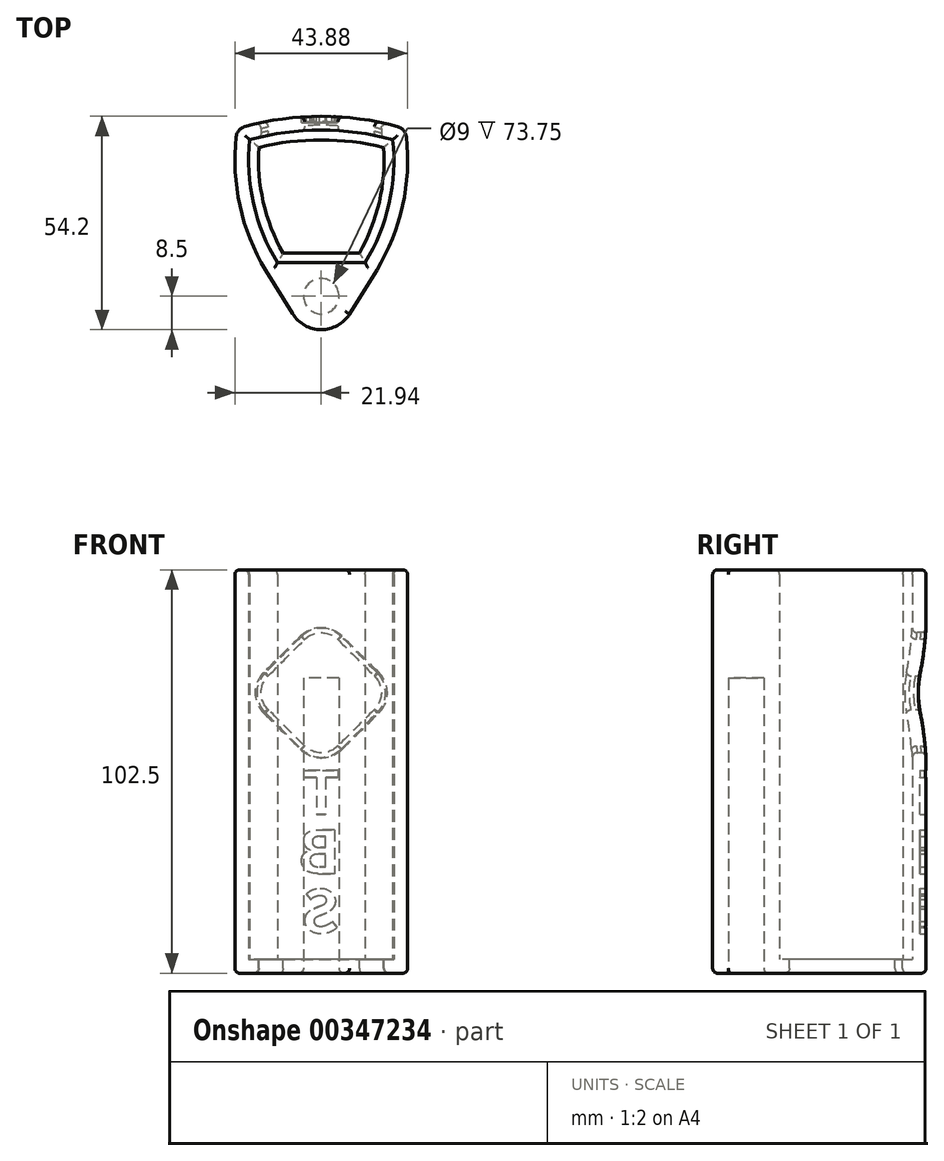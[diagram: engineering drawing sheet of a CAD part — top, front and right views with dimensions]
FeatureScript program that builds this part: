
annotation { "Feature Type Name" : "Feature", "Feature Type Description" : "" }
export const myFeature = defineFeature(function(context is Context, id is Id, definition is map)
    precondition{}
    {
        {
            var Q0;
            Q0=qCreatedBy(makeId("Top.planeOp"),FACE);
            var sketch = newSketch(context, id + "F0", { "sketchPlane" : qUnion([Q0])});
            skLineSegment(sketch, "E0", {"start": v(0, 0) * mm, "end": v(11.12, 0) * mm});
            skLineSegment(sketch, "E1", {"start": v(11.12, 0) * mm, "end": v(-11.12, 0) * mm});
            skArc(sketch, "E2", {"start": v(-18.16, 31.28) * mm, "mid": v(-17.22, 15.06) * mm, "end": v(-11.13, 0) * mm});
            skArc(sketch, "E3", {"start": v(11.13, 0) * mm, "mid": v(17.22, 15.06) * mm, "end": v(18.16, 31.28) * mm});
            skArc(sketch, "E4", {"start": v(18.16, 31.28) * mm, "mid": v(0, 33.7) * mm, "end": v(-18.16, 31.28) * mm});
            skArc(sketch, "E5.0", {"start": v(-21.34, 34) * mm, "mid": v(-20.88, 15.46) * mm, "end": v(-14.11, -1.82) * mm});
            skArc(sketch, "E5.1", {"start": v(21.34, 34) * mm, "mid": v(0, 37.2) * mm, "end": v(-21.34, 34) * mm});
            skArc(sketch, "E5.2", {"start": v(14.11, -1.82) * mm, "mid": v(20.88, 15.46) * mm, "end": v(21.34, 34) * mm});
            skCircle(sketch, "E6", {"center": v(0, -8.5) * mm, "radius": 4.5 * mm});
            skLineSegment(sketch, "E7", {"start": v(-14.11, -1.82) * mm, "end": v(-7.23, -12.97) * mm});
            skLineSegment(sketch, "E8", {"start": v(7.19, -13.03) * mm, "end": v(14.11, -1.82) * mm});
            skArc(sketch, "E9", {"start": v(-7.23, -12.97) * mm, "mid": v(-0.04, -17) * mm, "end": v(7.19, -13.03) * mm});
            skLineSegment(sketch, "E10", {"start": v(21.34, 34) * mm, "end": v(21.34, 39.15) * mm});
            skLineSegment(sketch, "E11", {"start": v(21.34, 39.15) * mm, "end": v(-21.34, 39.15) * mm});
            skLineSegment(sketch, "E12", {"start": v(-21.34, 39.15) * mm, "end": v(-21.34, 34) * mm});
            skSolve(sketch);
        }
        {
            var Q0;
            {var subQ3=sQuery(id+"F0.wireOp",EDGE,"E2");Q0=makeQuery(id+"F0.imprint","IMPRINT",FACE,{"disambiguationData":[TD([[makeQuery(id+"F0.imprint","IMPRINT",EDGE,{"derivedFrom":subQ3}),-1.0]])]});}
            var Q1;
            Q1=makeQuery(id+"F0.imprint","IMPRINT",FACE,{"disambiguationData":[TD([[makeQuery(id+"F0.imprint","IMPRINT",EDGE,{"derivedFrom":sQuery(id+"F0.wireOp",EDGE,"E6")}),1.0]])]});
            extrude(context, id + "F1", {"entities" : qUnion([Q0, Q1]), "depth" : 102.5 * mm});
        }
        {
            var Q0;
            {var subQ1=sQuery(id+"F0.wireOp",EDGE,"E2");Q0=makeQuery(id+"F0.imprint","IMPRINT",FACE,{"disambiguationData":[TD([[makeQuery(id+"F0.imprint","IMPRINT",EDGE,{"derivedFrom":subQ1}),1.0]])]});}
            extrude(context, id + "F2", {"entities" : qUnion([Q0]), "operationType" : NewBodyOperationType.ADD, "depth" : 3.5 * mm});
        }
        {
            var Q0;
            Q0=makeQuery(id+"F0.imprint","IMPRINT",FACE,{"disambiguationData":[TD([[makeQuery(id+"F0.imprint","IMPRINT",EDGE,{"derivedFrom":sQuery(id+"F0.wireOp",EDGE,"E6")}),1.0]])]});
            extrude(context, id + "F3", {"entities" : qUnion([Q0]), "operationType" : NewBodyOperationType.REMOVE, "depth" : 75 * mm});
        }
        {
            var Q0;
            Q0=makeQuery(id+"F0.imprint","IMPRINT",FACE,{"disambiguationData":[TD([[makeQuery(id+"F0.imprint","IMPRINT",EDGE,{"derivedFrom":sQuery(id+"F0.wireOp",EDGE,"E5.1")}),-1.0]])]});
            extrude(context, id + "F4", {"entities" : qUnion([Q0]), "operationType" : NewBodyOperationType.ADD, "depth" : 102.5 * mm});
        }
        {
            var Q0;
            Q0=makeQuery(id+"F4.opExtrude","SWEPT_FACE",FACE,{"disambiguationData":[OSD([sQuery(id+"F0.wireOp",EDGE,"E11")])]});
            var sketch = newSketch(context, id + "F5", { "sketchPlane" : qUnion([Q0])});
            skPoint(sketch, "E13.endSnap0", {"position": v(0, 0) * mm});
            skLineSegment(sketch, "E14", {"start": v(-17.75, 71.25) * mm, "end": v(0, 89) * mm});
            skLineSegment(sketch, "E15", {"start": v(17.75, 71.25) * mm, "end": v(0, 53.5) * mm});
            skLineSegment(sketch, "E16", {"start": v(0, 53.5) * mm, "end": v(-17.75, 71.25) * mm});
            skLineSegment(sketch, "E17", {"start": v(0, 89) * mm, "end": v(17.75, 71.25) * mm});
            skSolve(sketch);
        }
        {
            var Q0;
            Q0=makeQuery(id+"F5.imprint","IMPRINT",FACE,{"disambiguationData":[TD([[makeQuery(id+"F5.imprint","IMPRINT",EDGE,{"derivedFrom":sQuery(id+"F5.wireOp",EDGE,"E14")}),-1.0]])]});
            extrude(context, id + "F6", {"entities" : qUnion([Q0]), "operationType" : NewBodyOperationType.REMOVE, "oppositeDirection" : true, "depth" : 10 * mm});
        }
        {
            var Q0;
            Q0=makeQuery(id+"F6.boolean.opBoolean","COPY",EDGE,{"derivedFrom":makeQuery(id+"F6.opExtrude","SWEPT_EDGE",EDGE,{"disambiguationData":[OSD([sQuery(id+"F5.wireOp",EDGE,"E15"),sQuery(id+"F5.wireOp",EDGE,"E17")])]})});
            var Q1;
            Q1=makeQuery(id+"F6.boolean.opBoolean","COPY",EDGE,{"derivedFrom":makeQuery(id+"F6.opExtrude","SWEPT_EDGE",EDGE,{"disambiguationData":[OSD([sQuery(id+"F5.wireOp",EDGE,"E15"),sQuery(id+"F5.wireOp",EDGE,"E16")])]})});
            var Q2;
            Q2=makeQuery(id+"F6.boolean.opBoolean","COPY",EDGE,{"derivedFrom":makeQuery(id+"F6.opExtrude","SWEPT_EDGE",EDGE,{"disambiguationData":[OSD([sQuery(id+"F5.wireOp",EDGE,"E14"),sQuery(id+"F5.wireOp",EDGE,"E16")])]})});
            var Q3;
            Q3=makeQuery(id+"F6.boolean.opBoolean","COPY",EDGE,{"derivedFrom":makeQuery(id+"F6.opExtrude","SWEPT_EDGE",EDGE,{"disambiguationData":[OSD([sQuery(id+"F5.wireOp",EDGE,"E14"),sQuery(id+"F5.wireOp",EDGE,"E17")])]})});
            fillet(context, id + "F7", {"entities" : qUnion([Q0, Q1, Q2, Q3]), "radius" : 6 * mm, "tangentPropagation" : true, "allowEdgeOverflow" : false});
        }
        {
            var Q0;
            Q0=makeQuery(id+"F4.opExtrude","SWEPT_FACE",FACE,{"disambiguationData":[OSD([sQuery(id+"F0.wireOp",EDGE,"E11")])]});
            var sketch = newSketch(context, id + "F8", { "sketchPlane" : qUnion([Q0])});
            skText(sketch, "E18", { "text": "T\nB\nS", "fontName": "NotoSansCJKsc-Bold.otf"});
            skPoint(sketch, "E18.firstSnap0", {"position": v(-21.34, 51.25) * mm});
            const initialGuessF8  = {"E18": [-0.00469, 0.04038, 1, 0, 0.01087]};
            skSetInitialGuess(sketch, initialGuessF8);
            skSolve(sketch);
        }
        {
            var Q0;
            Q0=qSketchRegion(id+"F8",true);
            extrude(context, id + "F9", {"entities" : qUnion([Q0]), "operationType" : NewBodyOperationType.REMOVE, "oppositeDirection" : true, "depth" : 4 * mm});
        }
        {
            var Q0;
            Q0=makeQuery(id+"F0.imprint","IMPRINT",FACE,{"disambiguationData":[TD([[makeQuery(id+"F0.imprint","IMPRINT",EDGE,{"derivedFrom":sQuery(id+"F0.wireOp",EDGE,"E5.1")}),-1.0]])]});
            extrude(context, id + "F10", {"entities" : qUnion([Q0]), "operationType" : NewBodyOperationType.REMOVE, "depth" : 102.5 * mm});
        }
        {
            var Q0;
            Q0=makeQuery(id+"F9.boolean.opBoolean","COPY",FACE,{"derivedFrom":makeQuery(id+"F9.opExtrude","CAP_FACE",FACE,{"disambiguationData":[OSD([sQuery(id+"F8.wireOp",EDGE,"E18.sketch_text.stroke-0"),sQuery(id+"F8.wireOp",EDGE,"E18.sketch_text.stroke-1"),sQuery(id+"F8.wireOp",EDGE,"E18.sketch_text.stroke-2"),sQuery(id+"F8.wireOp",EDGE,"E18.sketch_text.stroke-3"),sQuery(id+"F8.wireOp",EDGE,"E18.sketch_text.stroke-4"),sQuery(id+"F8.wireOp",EDGE,"E18.sketch_text.stroke-5"),sQuery(id+"F8.wireOp",EDGE,"E18.sketch_text.stroke-6"),sQuery(id+"F8.wireOp",EDGE,"E18.sketch_text.stroke-7")])],"isStart":false})});
            var Q1;
            Q1=makeQuery(id+"F9.boolean.opBoolean","COPY",FACE,{"derivedFrom":makeQuery(id+"F9.opExtrude","CAP_FACE",FACE,{"disambiguationData":[OSD([sQuery(id+"F8.wireOp",EDGE,"E18.sketch_text.stroke-8"),sQuery(id+"F8.wireOp",EDGE,"E18.sketch_text.stroke-9"),sQuery(id+"F8.wireOp",EDGE,"E18.sketch_text.stroke-10"),sQuery(id+"F8.wireOp",EDGE,"E18.sketch_text.stroke-11"),sQuery(id+"F8.wireOp",EDGE,"E18.sketch_text.stroke-12"),sQuery(id+"F8.wireOp",EDGE,"E18.sketch_text.stroke-13"),sQuery(id+"F8.wireOp",EDGE,"E18.sketch_text.stroke-14"),sQuery(id+"F8.wireOp",EDGE,"E18.sketch_text.stroke-15"),sQuery(id+"F8.wireOp",EDGE,"E18.sketch_text.stroke-16"),sQuery(id+"F8.wireOp",EDGE,"E18.sketch_text.stroke-17"),sQuery(id+"F8.wireOp",EDGE,"E18.sketch_text.stroke-18"),sQuery(id+"F8.wireOp",EDGE,"E18.sketch_text.stroke-19"),sQuery(id+"F8.wireOp",EDGE,"E18.sketch_text.stroke-20"),sQuery(id+"F8.wireOp",EDGE,"E18.sketch_text.stroke-21"),sQuery(id+"F8.wireOp",EDGE,"E18.sketch_text.stroke-22"),sQuery(id+"F8.wireOp",EDGE,"E18.sketch_text.stroke-23"),sQuery(id+"F8.wireOp",EDGE,"E18.sketch_text.stroke-24"),sQuery(id+"F8.wireOp",EDGE,"E18.sketch_text.stroke-25")])],"isStart":false})});
            var Q2;
            Q2=makeQuery(id+"F9.boolean.opBoolean","COPY",FACE,{"derivedFrom":makeQuery(id+"F9.opExtrude","CAP_FACE",FACE,{"disambiguationData":[OSD([sQuery(id+"F8.wireOp",EDGE,"E18.sketch_text.stroke-26"),sQuery(id+"F8.wireOp",EDGE,"E18.sketch_text.stroke-27"),sQuery(id+"F8.wireOp",EDGE,"E18.sketch_text.stroke-28"),sQuery(id+"F8.wireOp",EDGE,"E18.sketch_text.stroke-29"),sQuery(id+"F8.wireOp",EDGE,"E18.sketch_text.stroke-30"),sQuery(id+"F8.wireOp",EDGE,"E18.sketch_text.stroke-31"),sQuery(id+"F8.wireOp",EDGE,"E18.sketch_text.stroke-32"),sQuery(id+"F8.wireOp",EDGE,"E18.sketch_text.stroke-33"),sQuery(id+"F8.wireOp",EDGE,"E18.sketch_text.stroke-34"),sQuery(id+"F8.wireOp",EDGE,"E18.sketch_text.stroke-35"),sQuery(id+"F8.wireOp",EDGE,"E18.sketch_text.stroke-36"),sQuery(id+"F8.wireOp",EDGE,"E18.sketch_text.stroke-37"),sQuery(id+"F8.wireOp",EDGE,"E18.sketch_text.stroke-38"),sQuery(id+"F8.wireOp",EDGE,"E18.sketch_text.stroke-39"),sQuery(id+"F8.wireOp",EDGE,"E18.sketch_text.stroke-40"),sQuery(id+"F8.wireOp",EDGE,"E18.sketch_text.stroke-41")])],"isStart":false})});
            extrude(context, id + "F11", {"entities" : qUnion([Q0, Q1, Q2]), "operationType" : NewBodyOperationType.ADD, "depth" : .5 * mm});
        }
        {
            var Q0;
            {var subQ0=sQuery(id+"F0.wireOp",EDGE,"E12");var subQ1=sQuery(id+"F0.wireOp",EDGE,"E5.1");var subQ2=sQuery(id+"F0.wireOp",EDGE,"E5.0");Q0=makeQuery(id+"F10.boolean.opBoolean","MERGE",EDGE,{"derivedFrom":[makeQuery(id+"F4.boolean.opBoolean","MERGE",EDGE,{"derivedFrom":[makeQuery(id+"F1.opExtrude","SWEPT_EDGE",EDGE,{"disambiguationData":[OSD([subQ2,subQ1,subQ0])]}),makeQuery(id+"F4.opExtrude","SWEPT_EDGE",EDGE,{"disambiguationData":[OSD([subQ2,subQ1,subQ0])]})]}),makeQuery(id+"F10.opExtrude","SWEPT_EDGE",EDGE,{"disambiguationData":[OSD([subQ2,subQ1,subQ0])]})]});}
            var Q1;
            {var subQ0=sQuery(id+"F0.wireOp",EDGE,"E10");var subQ1=sQuery(id+"F0.wireOp",EDGE,"E5.2");var subQ2=sQuery(id+"F0.wireOp",EDGE,"E5.1");Q1=makeQuery(id+"F10.boolean.opBoolean","MERGE",EDGE,{"derivedFrom":[makeQuery(id+"F4.boolean.opBoolean","MERGE",EDGE,{"derivedFrom":[makeQuery(id+"F1.opExtrude","SWEPT_EDGE",EDGE,{"disambiguationData":[OSD([subQ2,subQ1,subQ0])]}),makeQuery(id+"F4.opExtrude","SWEPT_EDGE",EDGE,{"disambiguationData":[OSD([subQ2,subQ1,subQ0])]})]}),makeQuery(id+"F10.opExtrude","SWEPT_EDGE",EDGE,{"disambiguationData":[OSD([subQ2,subQ1,subQ0])]})]});}
            fillet(context, id + "F12", {"entities" : qUnion([Q0, Q1]), "radius" : 3 * mm, "tangentPropagation" : true, "allowEdgeOverflow" : false});
        }
        {
            var Q0;
            Q0=makeQuery(id+"F2.opExtrude","CAP_FACE",FACE,{"disambiguationData":[OSD([sQuery(id+"F0.wireOp",EDGE,"E1"),sQuery(id+"F0.wireOp",EDGE,"E2"),sQuery(id+"F0.wireOp",EDGE,"E3"),sQuery(id+"F0.wireOp",EDGE,"E4")])],"isStart":false});
            var sketch = newSketch(context, id + "F13", { "sketchPlane" : qUnion([Q0])});
            skArc(sketch, "E19.0", {"start": v(9.7, 2.5) * mm, "mid": v(14.75, 15.45) * mm, "end": v(15.83, 29.3) * mm});
            skLineSegment(sketch, "E19.1", {"start": v(-9.7, 2.5) * mm, "end": v(9.7, 2.5) * mm});
            skArc(sketch, "E19.2", {"start": v(-15.83, 29.3) * mm, "mid": v(-14.75, 15.45) * mm, "end": v(-9.7, 2.5) * mm});
            skArc(sketch, "E19.3", {"start": v(15.83, 29.3) * mm, "mid": v(0, 31.2) * mm, "end": v(-15.83, 29.3) * mm});
            skSolve(sketch);
        }
        {
            var Q0;
            Q0=makeQuery(id+"F13.imprint","IMPRINT",FACE,{"disambiguationData":[TD([[makeQuery(id+"F13.imprint","IMPRINT",EDGE,{"derivedFrom":sQuery(id+"F13.wireOp",EDGE,"E19.0")}),1.0]])]});
            extrude(context, id + "F14", {"entities" : qUnion([Q0]), "operationType" : NewBodyOperationType.REMOVE, "oppositeDirection" : true, "depth" : 25 * mm});
        }
        {
            var Q0;
            {var subQ0=sQuery(id+"F0.wireOp",EDGE,"E5.1");var subQ1=sQuery(id+"F0.wireOp",EDGE,"E4");var subQ2=sQuery(id+"F0.wireOp",EDGE,"E3");var subQ3=sQuery(id+"F0.wireOp",EDGE,"E2");var subQ4=sQuery(id+"F0.wireOp",EDGE,"E1");Q0=makeQuery(id+"F4.boolean.opBoolean","MERGE",FACE,{"derivedFrom":[makeQuery(id+"F2.boolean.opBoolean","MERGE",FACE,{"derivedFrom":[makeQuery(id+"F1.opExtrude","CAP_FACE",FACE,{"disambiguationData":[OSD([subQ4,subQ3,subQ2,subQ1,sQuery(id+"F0.wireOp",EDGE,"E5.0"),subQ0,sQuery(id+"F0.wireOp",EDGE,"E5.2"),sQuery(id+"F0.wireOp",EDGE,"E7"),sQuery(id+"F0.wireOp",EDGE,"E8"),sQuery(id+"F0.wireOp",EDGE,"E9")])],"isStart":true}),makeQuery(id+"F2.opExtrude","CAP_FACE",FACE,{"disambiguationData":[OSD([subQ4,subQ3,subQ2,subQ1])],"isStart":true})]}),makeQuery(id+"F4.opExtrude","CAP_FACE",FACE,{"disambiguationData":[OSD([subQ0,sQuery(id+"F0.wireOp",EDGE,"E10"),sQuery(id+"F0.wireOp",EDGE,"E11"),sQuery(id+"F0.wireOp",EDGE,"E12")])],"isStart":true})]});}
            fillet(context, id + "F15", {"entities" : qUnion([Q0]), "radius" : 1.25 * mm, "tangentPropagation" : true, "allowEdgeOverflow" : false});
        }
        {
            var Q0;
            {var subQ0=sQuery(id+"F0.wireOp",EDGE,"E5.1");Q0=makeQuery(id+"F4.boolean.opBoolean","MERGE",FACE,{"derivedFrom":[makeQuery(id+"F1.opExtrude","CAP_FACE",FACE,{"disambiguationData":[OSD([sQuery(id+"F0.wireOp",EDGE,"E1"),sQuery(id+"F0.wireOp",EDGE,"E2"),sQuery(id+"F0.wireOp",EDGE,"E3"),sQuery(id+"F0.wireOp",EDGE,"E4"),sQuery(id+"F0.wireOp",EDGE,"E5.0"),subQ0,sQuery(id+"F0.wireOp",EDGE,"E5.2"),sQuery(id+"F0.wireOp",EDGE,"E7"),sQuery(id+"F0.wireOp",EDGE,"E8"),sQuery(id+"F0.wireOp",EDGE,"E9")])],"isStart":false}),makeQuery(id+"F4.opExtrude","CAP_FACE",FACE,{"disambiguationData":[OSD([subQ0,sQuery(id+"F0.wireOp",EDGE,"E10"),sQuery(id+"F0.wireOp",EDGE,"E11"),sQuery(id+"F0.wireOp",EDGE,"E12")])],"isStart":false})]});}
            fillet(context, id + "F16", {"entities" : qUnion([Q0]), "radius" : 1.25 * mm, "tangentPropagation" : true, "allowEdgeOverflow" : false});
        }
        {
            var Q0;
            Q0=makeQuery(id+"F10.boolean.opBoolean","INTERSECT",EDGE,{"derivedFrom":[makeQuery(id+"F7.opFillet","BLEND_FACE",FACE,{"disambiguationData":[OSD([sQuery(id+"F5.wireOp",EDGE,"E15"),sQuery(id+"F5.wireOp",EDGE,"E17")])]}),makeQuery(id+"F10.opExtrude","SWEPT_FACE",FACE,{"disambiguationData":[OSD([sQuery(id+"F0.wireOp",EDGE,"E5.1")])]})]});
            var Q1;
            Q1=makeQuery(id+"F7.opFillet","BLEND_EDGE",EDGE,{"blendedFrom":[makeQuery(id+"F6.boolean.opBoolean","COPY",EDGE,{"derivedFrom":makeQuery(id+"F6.opExtrude","SWEPT_EDGE",EDGE,{"disambiguationData":[OSD([sQuery(id+"F5.wireOp",EDGE,"E15"),sQuery(id+"F5.wireOp",EDGE,"E17")])]})}),makeQuery(id+"F1.opExtrude","SWEPT_FACE",FACE,{"disambiguationData":[OSD([sQuery(id+"F0.wireOp",EDGE,"E4")])]})],"blendedInto":[makeQuery(id+"F1.opExtrude","SWEPT_FACE",FACE,{"disambiguationData":[OSD([sQuery(id+"F0.wireOp",EDGE,"E4")])]})]});
            fillet(context, id + "F17", {"entities" : qUnion([Q0, Q1]), "radius" : 1.25 * mm, "tangentPropagation" : true, "allowEdgeOverflow" : false});
        }
    });
